# Revit family: Шкаф квартирный телекоммуникационный встраиваемый с радиопрозрачной дверцей ССД
name_source: partatom
category: Электрооборудование
revit_build: Autodesk Revit 2018 (Build: 20170927_1515(x64)
units: mm (PartAtom-declared; Revit-internal decimal feet)

## family parameters
Общий = Нет
Основа = Грань
При загрузке вырезать с полостями = Да
Размер круглого соединителя = Использовать диаметр
Тип детали = Другая панель
Точка расчета площади = Нет

## types (4) — shared parameters
Внимание!!! = Активная мощность выставляется в зависимости от
установленного оборудования связи, но не более 1 кВт.
Габаритные размеры (в сборе), мм = 447х447х100
Габаритные размеры (корпуса), мм = 394х394х80
394х394х80
394х394х80
394х394х80
Габаритные размеры (накладной крышки), мм = 447х447х20
Коэффициент мощности = 0.95
Отметка по умолчанию = 1500 мм
Спец.ЕдИзм = шт.
Спец.Изготовитель = ЗАО "СвязьСтройДеталь"
Спец.Количество = 1
Спец.НаименованиеИТехнХар = Шкаф квартирный телекоммуникационный встраиваемый с радиопрозрачной дверцей
Спец.Подраздел = Шкафы квартирные
Спец.РазделСпец = Шкафы и стойки телекоммуникационные
Ссылка на инструкцию изделия = https://www.ssd.ru
Ссылка на сайт производителя = https://www.ssd.ru

## per-type parameters (varying)
| type | Делитель 1х2 | Делитель 1х3 | Делитель 1х4 | Комплектность | Начинка ШТ-НСс | Описание изделия | Спец.КодОборудИзделияМатериала | Спец.ТипМаркаОбозначДокумента | Тип шкафа квартиного | УГО |
| Шкаф квартирный телекоммуникационный встраиваемый с радиопрозрачной дверцей ШТ-НСс пустой ССД | Нет | Нет | Нет | Корпус- 1 шт.
Накладная рамка с дверцей и замком - 1 шт.
Полка для роутера - 1 шт.
Монтажная панель с крепежом - 1 шт.
Патч-панель настенная на 12 портов с кронштейном	1 шт.
Розетка- 2 шт.
Провод заземления двери и корпуса- 1 шт.
Резиновая заглушка кабельного ввода - 6 шт.
Крепежная гайка М4- 4 шт.
Крепежная шайба М4 -4 шт | Нет | Предназначен для размещения пассивного и активного сетевого оборудования, в том числе с беспроводным доступом.

Оболочка шкафа состоит из корпуса и внешнего лючка с накладной рамкой и перфорированной дверцей с замком,
 изготовленные из стали толщиной 1,0 мм. Накладная рамка имеет возможность регулировки по глубине.
Дверца имеет перфорацию для охлаждения установленного внутри активного оборудования и прохождения радиосигнала от WI-FI роутера.
 Корпус шкафа с четырёх сторон, а также на задней стенке имеет выламываемые кабельные вводы диаметром 36 мм.
 В комплекте со шкафом поставляются 6 резиновых заглушек кабельного ввода. 
На каждой боковой стенке а также на задней стенке корпуса выполнены отверстия диаметром 8,5 мм для крепления шкафа в стене на дюбелях. 
На задней стенке внутри шкафа имеется регулируемая по высоте и выдвижению полка для установки WI-FI роутера (роутер в комплект на входит),
 монтажная панель, органайзер кабельный, кронштейн для разветвителя на 4 параллельных порта RJ-45 (разветвитель в комплект не входит).
 За полкой WI-FI роутера на задней стенке имеется крепёж для установки RF-усилителя (RF-усилитель в комплект не входит). 
На боковой стенке и в дне корпуса установлены силовые розетки. На двери и корпусе расположены элементы контура заземления.

Покрытие шкафа полимерное порошковое цвета RAL 9001. | 130411-01175 | ШТ-НСс пустой ССД | ШТ-НСс пустой ССД_LOD 200 | УГО_ШТ-НСс пустой ССД |
| Шкаф квартирный телекоммуникационный встраиваемый с радиопрозрачной дверцей ШТ-НСс 2+1 патч-корд, делитель 1х2 ССД | Да | Нет | Нет | Корпус - 1 шт.
Накладная рамка с дверцей и замком	- 1 шт.
Полка для роутера - 1 шт.
Монтажная панель с крепежом - 1 шт.
Патч-панель настенная на 12 портов с кронштейном	1 шт.
Розетка - 2 шт.
Провод заземления двери и корпуса - 1 шт.
Резиновая заглушка кабельного ввода  - 6 шт.
Крепежная гайка М4 - 4 шт.
Крепежная шайба М4 - 4 шт.
Патч-корд 0.3м зеленый - 1 шт.
Патч-корд 0.3м красный - 2 шт.
Делитель ТВ сигнала 1 вход 2 выхода - 1 шт. | Да | Предназначен для размещения пассивного и активного сетевого оборудования, в том числе с беспроводным доступом.

Оболочка шкафа состоит из корпуса и внешнего лючка с накладной рамкой и перфорированной дверцей с замком,
 изготовленные из стали толщиной 1,0 мм. Накладная рамка имеет возможность регулировки по глубине.
Дверца имеет перфорацию для охлаждения установленного внутри активного оборудования и прохождения радиосигнала от WI-FI роутера. 
Корпус шкафа с четырёх сторон, а также на задней стенке имеет выламываемые кабельные вводы диаметром 36 мм. 
В комплекте со шкафом поставляются 6 резиновых заглушек кабельного ввода. На каждой боковой стенке а также на задней стенке корпуса
 выполнены отверстия диаметром 8,5 мм для крепления шкафа в стене на дюбелях. На задней стенке внутри шкафа имеется регулируемая по высоте
и выдвижению полка для установки WI-FI роутера (роутер в комплект на входит), монтажная панель, органайзер кабельный, кронштейн для разветвителя
на 4 параллельных порта RJ-45 (разветвитель в комплект не входит). За полкой WI-FI роутера на задней стенке имеется крепёж для установки RF-усилителя (RF-усилитель в комплект не входит).
На боковой стенке и в дне корпуса установлены силовые розетки. На двери и корпусе расположены элементы контура заземления.

Покрытие шкафа полимерное порошковое цвета RAL 9001. | 130411-01176 | ШТ-НСс 2+1 патч-корд, делитель 1х2 ССД | ШТ-НСс 2 ССД_LOD 200 | УГО_ШТ-НСс 2 ССД |
| Шкаф квартирный телекоммуникационный встраиваемый с радиопрозрачной дверцей ШТ-НСс 3+2 патч-корда, делитель 1х3 ССД | Нет | Да | Нет | Корпус - 1 шт.
Накладная рамка с дверцей и замком	 - 1 шт.
Полка для роутера - 1 шт.
Монтажная панель с крепежом - 1 шт.
Патч-панель настенная на 12 портов с кронштейном - 1 шт.
Розетка - 2 шт.
Провод заземления двери и корпуса - 1 шт.
Резиновая заглушка кабельного ввода - 6 шт.
Крепежная гайка М4 - 4 шт.
Крепежная шайба М4 - 4 шт.
Патч-корд 0.3м зеленый - 2 шт.
Патч-корд 0.3м красный - 3 шт.
Делитель ТВ сигнала 1 вход 2 выхода - 1 шт.
Телефонный разветвитель 1 вход 4 выхода - 1 шт. | Да | Предназначен для размещения пассивного и активного сетевого оборудования, в том числе с беспроводным доступом.

Оболочка шкафа состоит из корпуса и внешнего лючка с накладной рамкой и перфорированной дверцей с замком,
 изготовленные из стали толщиной 1,0 мм. Накладная рамка имеет возможность регулировки по глубине.
Дверца имеет перфорацию для охлаждения установленного внутри активного оборудования и прохождения радиосигнала от WI-FI роутера.
 Корпус шкафа с четырёх сторон, а также на задней стенке имеет выламываемые кабельные вводы диаметром 36 мм.
 В комплекте со шкафом поставляются 6 резиновых заглушек кабельного ввода. 
На каждой боковой стенке а также на задней стенке корпуса выполнены отверстия диаметром 8,5 мм для крепления шкафа в стене на дюбелях. 
На задней стенке внутри шкафа имеется регулируемая по высоте и выдвижению полка для установки WI-FI роутера (роутер в комплект на входит),
 монтажная панель, органайзер кабельный, кронштейн для разветвителя на 4 параллельных порта RJ-45 (разветвитель в комплект не входит).
 За полкой WI-FI роутера на задней стенке имеется крепёж для установки RF-усилителя (RF-усилитель в комплект не входит). 
На боковой стенке и в дне корпуса установлены силовые розетки. На двери и корпусе расположены элементы контура заземления.

Покрытие шкафа полимерное порошковое цвета RAL 9001. | 130411-01177 | ШТ-НСс 3+2 патч-корда, делитель 1х3 ССД | ШТ-НСс 3 ССД_LOD 200 | УГО_ШТ-НСс 3 ССД |
| Шкаф квартирный телекоммуникационный встраиваемый с радиопрозрачной дверцей ШТ-НСс 4+3 патч-корда, делитель 1х4 ССД | Нет | Нет | Да | Корпус - 1 шт.
Накладная рамка с дверцей и замком	 -1 шт.
Полка для роутера - 1 шт.
Монтажная панель с крепежом - 1 шт.
Патч-панель настенная на 12 портов с кронштейном - 1 шт.
Розетка - 2 шт.
Провод заземления двери и корпуса - 1 шт.
Резиновая заглушка кабельного ввода - 6 шт.
Крепежная гайка М4 - 4 шт.
Крепежная шайба М4 - 4 шт.
Патч-корд 0.3м зеленый - 3 шт.
Патч-корд 0.3м красный - 4 шт.
Делитель ТВ сигнала 1 вход 2 выхода - 1 шт.
Телефонный разветвитель 1 вход 4 выхода -1 шт. | Да | Предназначен для размещения пассивного и активного сетевого оборудования,
в том числе с беспроводным доступом.

Оболочка шкафа состоит из корпуса и внешнего лючка с накладной рамкой и перфорированной дверцей с замком,
изготовленные из стали толщиной 1,0 мм. Накладная рамка имеет возможность регулировки по глубине.
Дверца имеет перфорацию для охлаждения установленного внутри активного оборудования и прохождения радиосигнала от WI-FI роутера. 
Корпус шкафа с четырёх сторон, а также на задней стенке имеет выламываемые кабельные вводы диаметром 36 мм. В комплекте со шкафом поставляются 6 резиновых заглушек кабельного ввода.
На каждой боковой стенке а также на задней стенке корпуса выполнены отверстия диаметром 8,5 мм для крепления шкафа в стене на дюбелях.
На задней стенке внутри шкафа имеется регулируемая по высоте и выдвижению полка для установки WI-FI роутера (роутер в комплект на входит), монтажная панель, органайзер кабельный, кронштейн для разветвителя на 4 параллельных порта RJ-45. 
За полкой WI-FI роутера на задней стенке имеется крепёж для установки RF-усилителя (RF-усилитель в комплект не входит). На боковой стенке и в дне корпуса установлены силовые розетки. На двери и корпусе расположены элементы контура заземления.

Покрытие шкафа полимерное порошковое цвета RAL 9001. | 130411-01178 | ШТ-НСс 4+3 патч-корда, делитель 1х4 ССД | ШТ-НСс 4 ССД_LOD 200 | УГО_ШТ-НСс 4 ССД |
